# Revit family: Electrical_Equipment-Poke_Through-Hubbell_Wiring-System_One-S1R8
name_source: partatom
category: Electrical Fixtures
revit_build: Autodesk Revit 2015 (Build: 20140606_1530(x64)
units: mm (PartAtom-declared; Revit-internal decimal feet)

## types (2) — shared parameters
Amperage Max Limit Note = Max (5) 20 Amp Duplex Circuit
Assembly Code = D5020115
Center Bottom Power = 2400 VA
Center Bottom Subplate = Center Subplate : S1R8CSPK
Center Middle Power = 2400 VA
Center Middle Subplate = Center Subplate : S1R8CSPK
Center Top Power = 2400 VA
Center Top Subplate = Center Subplate : S1R8CSPK
Conduit Connector 1 Description = Conduit Connector 1
Conduit Connector 2 Description = Conduit Connector 1
Conduit Connector 3 Description = Conduit Connector 1
Conduit Connector 4 Description = Conduit Connector 1
Conduit Connector 5 Description = Conduit Connector 1
Cover Material = Metal-Hubbell-Aluminum
Default Elevation = 0' - 0"
Description = System One - 8" Poke Through
Electrical Connector Description = Power Connector
Hardware Material = Metal-Hubbell-Steel
Left Side Power = 2400 VA
Left Side Subplate = Left Subplate : S1R8PSPZ
Load Classification = Power
Manufacturer = Hubbell-Wiring
Model = S1R8PT
Number of Poles = 1
Power Factor = 1
Product Documentation Link = http://ecatalog.hubbell-wiring.com
Product Page URL = http://ecatalog.hubbell-wiring.com
Product data url = https://bimobject.com
Right Connector = 0' - 0 17/32"
Right Side Power = 2400 VA
Right Side Subplate = Right Subplate : S1R8PSPZ
URL = http://www.hubbell-wiring.com
Voltage = 120 V

## per-type parameters (varying)
| type | Junction Box | Left Connector |
| S1R8JNC1 Junction Box | S1R8JNC1 : Junction Box | 0' - 0 13/16" |
| S1R8JNC2 Junction Box | S1R8JNC2 : Junction Box | 0' - 0 17/32" |

## geometry (parser evidence)
native form markers: Blend x28, Sweep x29
no freeform markers — native parametric forms only
